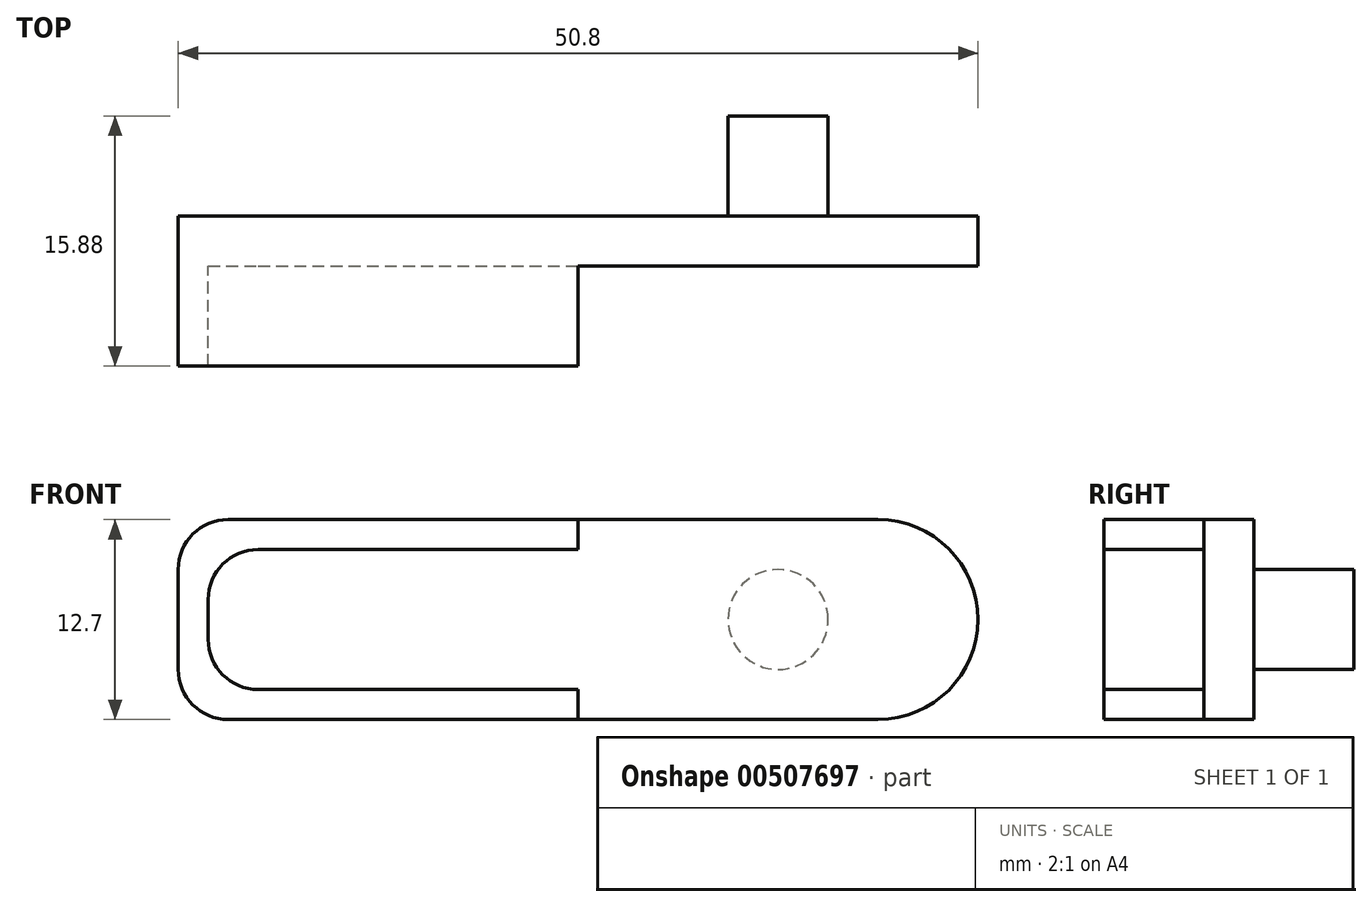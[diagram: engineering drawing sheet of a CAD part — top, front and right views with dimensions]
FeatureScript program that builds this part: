
annotation { "Feature Type Name" : "Feature", "Feature Type Description" : "" }
export const myFeature = defineFeature(function(context is Context, id is Id, definition is map)
    precondition{}
    {
        {
            var Q0;
            Q0=qCreatedBy(makeId("Front.planeOp"),FACE);
            var sketch = newSketch(context, id + "F0", { "sketchPlane" : qUnion([Q0])});
            skLineSegment(sketch, "E0.bottom", {"start": v(0, 0) * mm, "end": v(50.8, 0) * mm});
            skLineSegment(sketch, "E0.top", {"start": v(0, 12.7) * mm, "end": v(50.8, 12.7) * mm});
            skLineSegment(sketch, "E0.left", {"start": v(0, 0) * mm, "end": v(0, 12.7) * mm});
            skLineSegment(sketch, "E0.right", {"start": v(50.8, 0) * mm, "end": v(50.8, 12.7) * mm});
            skSolve(sketch);
        }
        {
            var Q0;
            Q0=makeQuery(id+"F0.imprint","IMPRINT",FACE,{"disambiguationData":[TD([[makeQuery(id+"F0.imprint","IMPRINT",EDGE,{"derivedFrom":sQuery(id+"F0.wireOp",EDGE,"E0.bottom")}),1.0]])]});
            extrude(context, id + "F1", {"entities" : qUnion([Q0]), "depth" : 3.17 * mm, "offsetDistance" : 25.4 * mm});
        }
        {
            var Q0;
            Q0=makeQuery(id+"F1.opExtrude","CAP_FACE",FACE,{"disambiguationData":[OSD([sQuery(id+"F0.wireOp",EDGE,"E0.bottom"),sQuery(id+"F0.wireOp",EDGE,"E0.top"),sQuery(id+"F0.wireOp",EDGE,"E0.left"),sQuery(id+"F0.wireOp",EDGE,"E0.right")])],"isStart":true});
            var sketch = newSketch(context, id + "F2", { "sketchPlane" : qUnion([Q0])});
            skPoint(sketch, "E1", {"position": v(-50.8, 6.35) * mm});
            skPoint(sketch, "E2", {"position": v(-38.1, 6.35) * mm});
            skCircle(sketch, "E3", {"center": v(-38.1, 6.35) * mm, "radius": 3.18 * mm});
            skSolve(sketch);
        }
        {
            var Q0;
            Q0=makeQuery(id+"F2.imprint","IMPRINT",FACE,{"disambiguationData":[TD([[makeQuery(id+"F2.imprint","IMPRINT",EDGE,{"derivedFrom":sQuery(id+"F2.wireOp",EDGE,"E3")}),1.0]])]});
            extrude(context, id + "F3", {"entities" : qUnion([Q0]), "operationType" : NewBodyOperationType.ADD, "depth" : 6.35 * mm, "offsetDistance" : 25.4 * mm});
        }
        {
            var Q0;
            Q0=makeQuery(id+"F1.opExtrude","CAP_FACE",FACE,{"disambiguationData":[OSD([sQuery(id+"F0.wireOp",EDGE,"E0.bottom"),sQuery(id+"F0.wireOp",EDGE,"E0.top"),sQuery(id+"F0.wireOp",EDGE,"E0.left"),sQuery(id+"F0.wireOp",EDGE,"E0.right")])],"isStart":false});
            var sketch = newSketch(context, id + "F4", { "sketchPlane" : qUnion([Q0])});
            skPoint(sketch, "E4", {"position": v(1.9, 10.8) * mm});
            skPoint(sketch, "E5", {"position": v(25.4, 10.8) * mm});
            skPoint(sketch, "E6", {"position": v(1.9, 1.9) * mm});
            skLineSegment(sketch, "E7", {"start": v(25.4, 12.7) * mm, "end": v(25.4, 10.8) * mm});
            skLineSegment(sketch, "E8", {"start": v(25.4, 10.8) * mm, "end": v(1.9, 10.8) * mm});
            skLineSegment(sketch, "E9", {"start": v(1.9, 10.8) * mm, "end": v(1.9, 1.9) * mm});
            skLineSegment(sketch, "E10", {"start": v(1.9, 1.9) * mm, "end": v(25.4, 1.9) * mm});
            skLineSegment(sketch, "E11", {"start": v(25.4, 1.9) * mm, "end": v(25.4, 0) * mm});
            skSolve(sketch);
        }
        {
            var Q0;
            {var subQ0=sQuery(id+"F4.wireOp",EDGE,"E7");Q0=makeQuery(id+"F4.imprint","IMPRINT",FACE,{"disambiguationData":[TD([[makeQuery(id+"F4.imprint","IMPRINT",EDGE,{"derivedFrom":subQ0}),-1.0]])]});}
            extrude(context, id + "F5", {"entities" : qUnion([Q0]), "operationType" : NewBodyOperationType.ADD, "depth" : 6.35 * mm, "offsetDistance" : 25.4 * mm});
        }
        {
            var Q0;
            Q0=makeQuery(id+"F1.opExtrude","SWEPT_EDGE",EDGE,{"disambiguationData":[OSD([sQuery(id+"F0.wireOp",EDGE,"E0.bottom"),sQuery(id+"F0.wireOp",EDGE,"E0.right")])]});
            var Q1;
            Q1=makeQuery(id+"F1.opExtrude","SWEPT_EDGE",EDGE,{"disambiguationData":[OSD([sQuery(id+"F0.wireOp",EDGE,"E0.top"),sQuery(id+"F0.wireOp",EDGE,"E0.right")])]});
            fillet(context, id + "F6", {"entities" : qUnion([Q0, Q1]), "radius" : 6.35 * mm, "tangentPropagation" : true, "allowEdgeOverflow" : false});
        }
        {
            var Q0;
            {var subQ0=sQuery(id+"F0.wireOp",EDGE,"E0.left");var subQ1=sQuery(id+"F0.wireOp",EDGE,"E0.top");Q0=makeQuery(id+"F5.boolean.opBoolean","MERGE",EDGE,{"derivedFrom":[makeQuery(id+"F1.opExtrude","SWEPT_EDGE",EDGE,{"disambiguationData":[OSD([subQ1,subQ0])]}),makeQuery(id+"F5.opExtrude","SWEPT_EDGE",EDGE,{"disambiguationData":[OSD([subQ1,subQ0])]})]});}
            var Q1;
            {var subQ0=sQuery(id+"F0.wireOp",EDGE,"E0.left");var subQ1=sQuery(id+"F0.wireOp",EDGE,"E0.bottom");Q1=makeQuery(id+"F5.boolean.opBoolean","MERGE",EDGE,{"derivedFrom":[makeQuery(id+"F1.opExtrude","SWEPT_EDGE",EDGE,{"disambiguationData":[OSD([subQ1,subQ0])]}),makeQuery(id+"F5.opExtrude","SWEPT_EDGE",EDGE,{"disambiguationData":[OSD([subQ1,subQ0])]})]});}
            var Q2;
            Q2=makeQuery(id+"F5.opExtrude","SWEPT_EDGE",EDGE,{"disambiguationData":[OSD([sQuery(id+"F4.wireOp",EDGE,"E8"),sQuery(id+"F4.wireOp",EDGE,"E9")])]});
            var Q3;
            Q3=makeQuery(id+"F5.opExtrude","SWEPT_EDGE",EDGE,{"disambiguationData":[OSD([sQuery(id+"F4.wireOp",EDGE,"E9"),sQuery(id+"F4.wireOp",EDGE,"E10")])]});
            fillet(context, id + "F7", {"entities" : qUnion([Q0, Q1, Q2, Q3]), "radius" : 3.17 * mm, "tangentPropagation" : true, "allowEdgeOverflow" : false});
        }
    });
